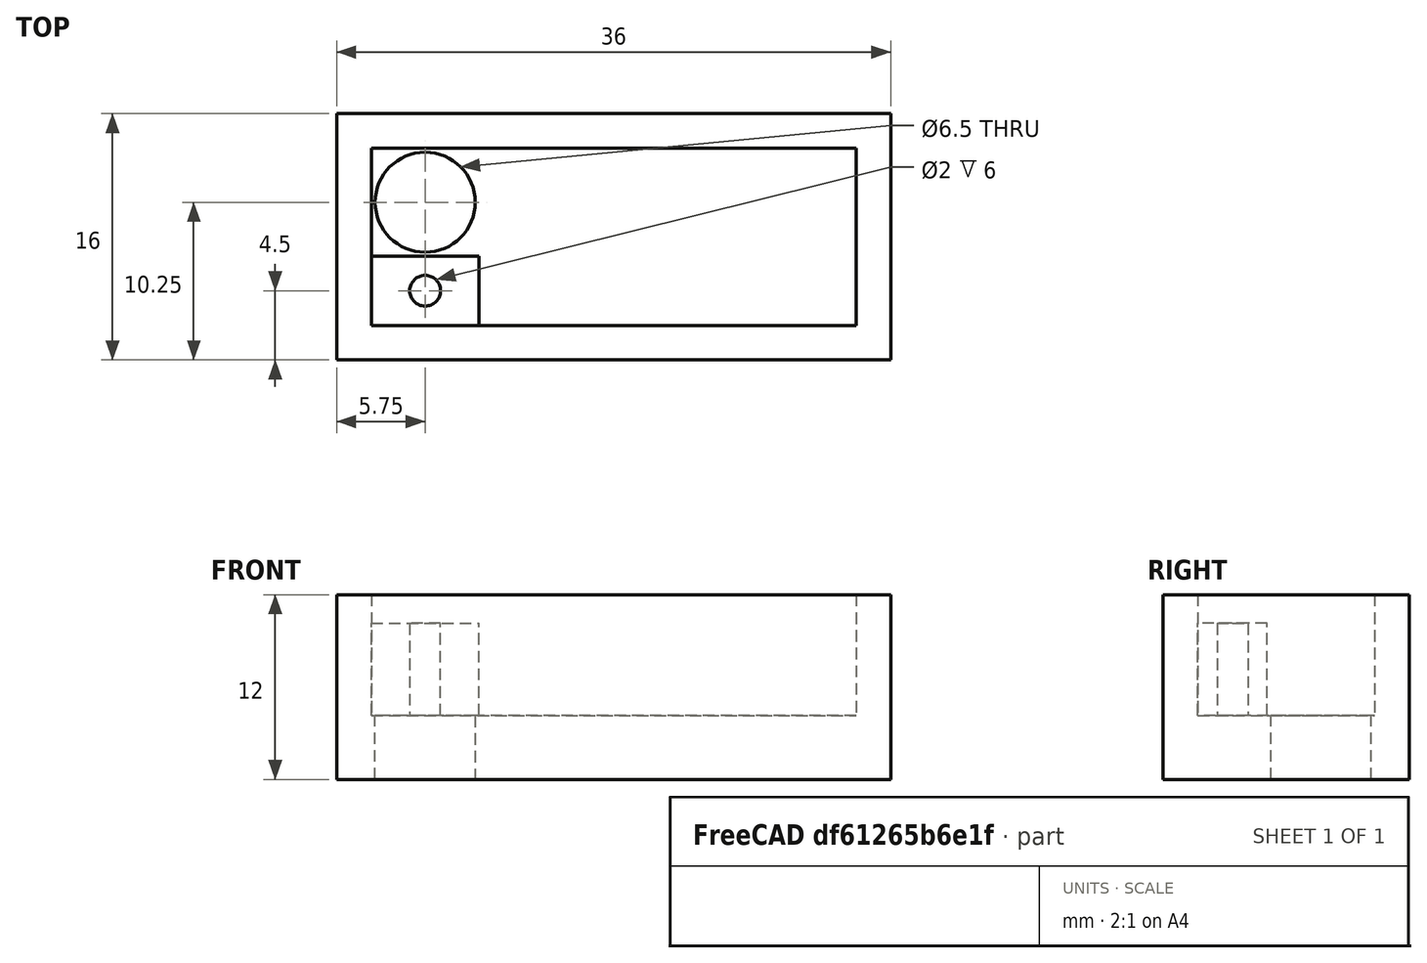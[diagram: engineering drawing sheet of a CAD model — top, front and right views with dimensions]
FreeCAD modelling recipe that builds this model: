
FCSTD DOCUMENT  (FreeCAD 0.19R24267 +148 (Git))
Label: LED Halterung
License: All rights reserved
LicenseURL: http://en.wikipedia.org/wiki/All_rights_reserved
objects: TechDraw::DrawViewDimension×14, Sketcher::SketchObject×4, TechDraw::DrawProjGroupItem×4, PartDesign::Pad×2, PartDesign::Pocket×2, PartDesign::Body×1, TechDraw::DrawSVGTemplate×1, TechDraw::DrawProjGroup×1, TechDraw::DrawPage×1
note: 13 computed .brp shape members not serialized (recipe doc carries the construction recipe); baked Part::Feature solids carry a one-line shape summary decoded from their .brp

FEATURE [Sketcher::SketchObject] Sketch
  FullyConstrained = true
  MapMode = 5
  Support = -> [XY_Plane]
  sketch-geometry (4):
    g0: LineSegment StartX=0 StartY=0 StartZ=0 EndX=36 EndY=0 EndZ=0
    g1: LineSegment StartX=36 StartY=0 StartZ=0 EndX=36 EndY=16 EndZ=0
    g2: LineSegment StartX=36 StartY=16 StartZ=0 EndX=0 EndY=16 EndZ=0
    g3: LineSegment StartX=0 StartY=16 StartZ=0 EndX=0 EndY=0 EndZ=0
  constraints (11):
    c: Coincident(g0,g1)
    c: Coincident(g1,g2)
    c: Coincident(g2,g3)
    c: Coincident(g3,g0)
    c: Horizontal(g0)
    c: Horizontal(g2)
    c: Vertical(g1)
    c: Vertical(g3)
    c: Coincident(g0,g-1)
    c: DistanceY(g3,g3) = 16
    c: DistanceX(g2,g2) = 36
FEATURE [PartDesign::Pad] Pad
  Direction = (1,1,1)
  Length = 12
  Length2 = 100
  Profile = -> Sketch
  Type = 0
FEATURE [Sketcher::SketchObject] Sketch001
  ExternalGeometry = -> [Pad]
  FullyConstrained = true
  MapMode = 5
  Placement = pos=(0,0,12) rot=(0,0,1;0rad)
  Support = -> [Pad]
  sketch-geometry (6):
    g0: LineSegment StartX=0 StartY=8 StartZ=0 EndX=36 EndY=8 EndZ=0
    g1: LineSegment StartX=18 StartY=16 StartZ=0 EndX=18 EndY=0 EndZ=0
    g2: LineSegment StartX=2.25 StartY=13.75 StartZ=0 EndX=33.75 EndY=13.75 EndZ=0
    g3: LineSegment StartX=33.75 StartY=13.75 StartZ=0 EndX=33.75 EndY=2.25 EndZ=0
    g4: LineSegment StartX=33.75 StartY=2.25 StartZ=0 EndX=2.25 EndY=2.25 EndZ=0
    g5: LineSegment StartX=2.25 StartY=2.25 StartZ=0 EndX=2.25 EndY=13.75 EndZ=0
  constraints (16):
    c: PointOnObject(g0,g-5)
    c: Horizontal(g0)
    c: PointOnObject(g1,g-3)
    c: Vertical(g1)
    c: Symmetric(g-1,g-4,g1)
    c: Symmetric(g-4,g-3,g0)
    c: Coincident(g2,g3)
    c: Coincident(g3,g4)
    c: Coincident(g4,g5)
    c: Coincident(g5,g2)
    c: Vertical(g5)
    c: Horizontal(g2)
    c: Symmetric(g3,g4,g1)
    c: Symmetric(g3,g2,g0)
    c: DistanceY(g2,g-5) = 2.25
    c: DistanceX(g-5,g2) = 2.25
FEATURE [PartDesign::Pocket] Pocket
  BaseFeature = -> Pad
  Length = 7.85
  Length2 = 100
  Profile = -> Sketch001
  Type = 0
FEATURE [Sketcher::SketchObject] Sketch002
  ExternalGeometry = -> [Pocket]
  FullyConstrained = true
  MapMode = 5
  Placement = pos=(0,0,4.15) rot=(0,0,1;0rad)
  Support = -> [Pocket]
  sketch-geometry (5):
    g0: LineSegment StartX=2.25 StartY=2.25 StartZ=0 EndX=9.25 EndY=2.25 EndZ=0
    g1: LineSegment StartX=9.25 StartY=2.25 StartZ=0 EndX=9.25 EndY=6.75 EndZ=0
    g2: LineSegment StartX=9.25 StartY=6.75 StartZ=0 EndX=2.25 EndY=6.75 EndZ=0
    g3: LineSegment StartX=2.25 StartY=6.75 StartZ=0 EndX=2.25 EndY=2.25 EndZ=0
    g4: Circle CenterX=5.75 CenterY=4.5 CenterZ=0 NormalX=0 NormalY=0 NormalZ=1 AngleXU=0 Radius=1
  constraints (13):
    c: Coincident(g0,g1)
    c: Coincident(g1,g2)
    c: Coincident(g2,g3)
    c: Coincident(g3,g0)
    c: Horizontal(g0)
    c: Horizontal(g2)
    c: Vertical(g1)
    c: Vertical(g3)
    c: Coincident(g0,g-5)
    c: DistanceY(g0,g4) = 2.25
    c: DistanceX(g0,g4) = 3.5
    c: Radius(g4) = 1
    c: Symmetric(g0,g1,g4)
FEATURE [PartDesign::Pad] Pad001
  BaseFeature = -> Pocket
  Direction = (1,1,1)
  Length = 6
  Length2 = 100
  Profile = -> Sketch002
  Type = 0
FEATURE [Sketcher::SketchObject] Sketch003
  ExternalGeometry = -> [Pad001]
  FullyConstrained = true
  MapMode = 5
  Placement = pos=(0,0,4.15) rot=(0,0,1;0rad)
  Support = -> [Pad001]
  sketch-geometry (1):
    g0: Circle CenterX=5.75 CenterY=10.25 CenterZ=0 NormalX=0 NormalY=0 NormalZ=1 AngleXU=0 Radius=3.25
  constraints (3):
    c: Vertical(g0,g-6)
    c: DistanceY(g0,g-5) = 3.5
    c: Radius(g0) = 3.25
FEATURE [PartDesign::Pocket] Pocket001
  BaseFeature = -> Pad001
  Length = 5
  Length2 = 100
  Profile = -> Sketch003
  Type = 0
FEATURE [PartDesign::Body] Body
  Group = -> [Sketch,Pad,Sketch001,Pocket,Sketch002,Pad001,Sketch003,Pocket001]
  Origin = -> Origin
  Tip = -> Pocket001
FEATURE [TechDraw::DrawSVGTemplate] Template
  EditableTexts = Designed_by_Name=David Völlm; Drawing_number=1; FC-Date=Date; FC-SC=1:1; FC-SH=1; FC-Title=LED-Halterung; Subtitle=Subtitle; Weight=Weight
  Height = 210
  Orientation = 1
  Width = 297
FEATURE [TechDraw::DrawProjGroupItem] ProjItem  label="Front"
  CoarseView = false
  Direction = (0,-1,0)
  Focus = 100
  HardHidden = false
  IsoCount = 0
  IsoHidden = false
  IsoVisible = false
  LockPosition = true
  Perspective = false
  Rotation = 0
  RotationVector = (1,0,0)
  ScaleType = 2
  SeamHidden = false
  SeamVisible = true
  SmoothHidden = false
  SmoothVisible = true
  Source = -> [Body]
  Type = 0
  X = 0
  XDirection = (1,0,0)
  Y = 0
FEATURE [TechDraw::DrawProjGroupItem] ProjItem001  label="Left"
  CoarseView = false
  Direction = (-1,-1e-16,0)
  Focus = 100
  HardHidden = false
  IsoCount = 0
  IsoHidden = false
  IsoVisible = false
  LockPosition = false
  Perspective = false
  Rotation = 0
  RotationVector = (1,0,0)
  ScaleType = 2
  SeamHidden = false
  SeamVisible = true
  SmoothHidden = false
  SmoothVisible = true
  Source = -> [Body]
  Type = 1
  X = 41
  XDirection = (1e-16,-1,0)
  Y = 0
FEATURE [TechDraw::DrawProjGroupItem] ProjItem002  label="Bottom"
  CoarseView = false
  Direction = (0,0,-1)
  Focus = 100
  HardHidden = false
  IsoCount = 0
  IsoHidden = false
  IsoVisible = false
  LockPosition = false
  Perspective = false
  Rotation = 0
  RotationVector = (1,0,0)
  ScaleType = 2
  SeamHidden = false
  SeamVisible = true
  SmoothHidden = false
  SmoothVisible = true
  Source = -> [Body]
  Type = 5
  X = 0
  XDirection = (1,0,0)
  Y = 31
FEATURE [TechDraw::DrawProjGroupItem] ProjItem003  label="Top"
  CoarseView = false
  Direction = (0,0,1)
  Focus = 100
  HardHidden = false
  IsoCount = 0
  IsoHidden = false
  IsoVisible = false
  LockPosition = false
  Perspective = false
  Rotation = 0
  RotationVector = (1,0,0)
  ScaleType = 2
  SeamHidden = false
  SeamVisible = true
  SmoothHidden = false
  SmoothVisible = true
  Source = -> [Body]
  Type = 4
  X = 0
  XDirection = (1,0,0)
  Y = -31
FEATURE [TechDraw::DrawProjGroup] ProjGroup
  Anchor = -> ProjItem
  AutoDistribute = true
  LockPosition = false
  ProjectionType = 0
  Rotation = 0
  ScaleType = 0
  Source = -> [Body]
  Views = -> [ProjItem,ProjItem001,ProjItem002,ProjItem003]
  X = 99.7152
  Y = 125.018
  spacingX = 15
  spacingY = 15
FEATURE [TechDraw::DrawViewDimension] Dimension
  Arbitrary = false
  ArbitraryTolerances = false
  EqualTolerance = true
  FormatSpec = R%.2f
  FormatSpecOverTolerance = %+.2f
  FormatSpecUnderTolerance = %+.2f
  Inverted = false
  LockPosition = false
  MeasureType = 1
  OverTolerance = 0
  References2D = -> [ProjItem002]
  Rotation = 0
  ScaleType = 0
  TheoreticalExact = false
  Type = 4
  UnderTolerance = 0
  X = 6.31337
  Y = 3.55127
FEATURE [TechDraw::DrawViewDimension] Dimension001
  Arbitrary = false
  ArbitraryTolerances = false
  EqualTolerance = true
  FormatSpec = %.2f
  FormatSpecOverTolerance = %+.2f
  FormatSpecUnderTolerance = %+.2f
  Inverted = false
  LockPosition = false
  MeasureType = 1
  OverTolerance = 0
  References2D = -> [ProjItem002]
  Rotation = 0
  ScaleType = 0
  TheoreticalExact = false
  Type = 2
  UnderTolerance = 0
  X = 25.1025
  Y = 1.97293
FEATURE [TechDraw::DrawViewDimension] Dimension002
  Arbitrary = false
  ArbitraryTolerances = false
  EqualTolerance = true
  FormatSpec = %.2f
  FormatSpecOverTolerance = %+.2f
  FormatSpecUnderTolerance = %+.2f
  Inverted = false
  LockPosition = false
  MeasureType = 1
  OverTolerance = 0
  References2D = -> [ProjItem002]
  Rotation = 0
  ScaleType = 0
  TheoreticalExact = false
  Type = 1
  UnderTolerance = 0
  X = -1.57834
  Y = 23.7834
FEATURE [TechDraw::DrawViewDimension] Dimension003
  Arbitrary = false
  ArbitraryTolerances = false
  EqualTolerance = true
  FormatSpec = %.2f
  FormatSpecOverTolerance = %+.2f
  FormatSpecUnderTolerance = %+.2f
  Inverted = false
  LockPosition = false
  MeasureType = 1
  OverTolerance = 0
  References2D = -> [ProjItem002]
  Rotation = 0
  ScaleType = 0
  TheoreticalExact = false
  Type = 1
  UnderTolerance = 0
  X = -13.8946
  Y = -13.0167
FEATURE [TechDraw::DrawViewDimension] Dimension004
  Arbitrary = false
  ArbitraryTolerances = false
  EqualTolerance = true
  FormatSpec = %.2f
  FormatSpecOverTolerance = %+.2f
  FormatSpecUnderTolerance = %+.2f
  Inverted = false
  LockPosition = false
  MeasureType = 1
  OverTolerance = 0
  References2D = -> [ProjItem002]
  Rotation = 0
  ScaleType = 0
  TheoreticalExact = false
  Type = 2
  UnderTolerance = 0
  X = -31.6509
  Y = 7.50174
FEATURE [TechDraw::DrawViewDimension] Dimension005
  Arbitrary = false
  ArbitraryTolerances = false
  EqualTolerance = true
  FormatSpec = %.2f
  FormatSpecOverTolerance = %+.2f
  FormatSpecUnderTolerance = %+.2f
  Inverted = false
  LockPosition = false
  MeasureType = 1
  OverTolerance = 0
  References2D = -> [ProjItem001]
  Rotation = 0
  ScaleType = 0
  TheoreticalExact = false
  Type = 2
  UnderTolerance = 0
  X = 15.8917
  Y = 1.18376
FEATURE [TechDraw::DrawViewDimension] Dimension006
  Arbitrary = false
  ArbitraryTolerances = false
  EqualTolerance = true
  FormatSpec = %.2f
  FormatSpecOverTolerance = %+.2f
  FormatSpecUnderTolerance = %+.2f
  Inverted = false
  LockPosition = false
  MeasureType = 1
  OverTolerance = 0
  References2D = -> [ProjItem003]
  Rotation = 0
  ScaleType = 0
  TheoreticalExact = false
  Type = 2
  UnderTolerance = 0
  X = 23.3023
  Y = 1.4631
FEATURE [TechDraw::DrawViewDimension] Dimension007
  Arbitrary = false
  ArbitraryTolerances = false
  EqualTolerance = true
  FormatSpec = %.2f
  FormatSpecOverTolerance = %+.2f
  FormatSpecUnderTolerance = %+.2f
  Inverted = false
  LockPosition = false
  MeasureType = 1
  OverTolerance = 0
  References2D = -> [ProjItem003]
  Rotation = 0
  ScaleType = 0
  TheoreticalExact = false
  Type = 2
  UnderTolerance = 0
  X = 34.246
  Y = -0.603869
FEATURE [TechDraw::DrawViewDimension] Dimension008
  Arbitrary = false
  ArbitraryTolerances = false
  EqualTolerance = true
  FormatSpec = %.2f
  FormatSpecOverTolerance = %+.2f
  FormatSpecUnderTolerance = %+.2f
  Inverted = false
  LockPosition = false
  MeasureType = 1
  OverTolerance = 0
  References2D = -> [ProjItem003]
  Rotation = 0
  ScaleType = 0
  TheoreticalExact = false
  Type = 1
  UnderTolerance = 0
  X = 10.7951
  Y = -9.48066
FEATURE [TechDraw::DrawViewDimension] Dimension009
  Arbitrary = false
  ArbitraryTolerances = false
  EqualTolerance = true
  FormatSpec = %.2f
  FormatSpecOverTolerance = %+.2f
  FormatSpecUnderTolerance = %+.2f
  Inverted = false
  LockPosition = false
  MeasureType = 1
  OverTolerance = 0
  References2D = -> [ProjItem003]
  Rotation = 0
  ScaleType = 0
  TheoreticalExact = false
  Type = 1
  UnderTolerance = 0
  X = 4.10387
  Y = -16.0816
FEATURE [TechDraw::DrawViewDimension] Dimension010
  Arbitrary = false
  ArbitraryTolerances = false
  EqualTolerance = true
  FormatSpec = %.2f
  FormatSpecOverTolerance = %+.2f
  FormatSpecUnderTolerance = %+.2f
  Inverted = false
  LockPosition = false
  MeasureType = 1
  OverTolerance = 0
  References2D = -> [ProjItem003]
  Rotation = 0
  ScaleType = 0
  TheoreticalExact = false
  Type = 1
  UnderTolerance = 0
  X = 2.68016
  Y = -24.5107
FEATURE [TechDraw::DrawViewDimension] Dimension011
  Arbitrary = false
  ArbitraryTolerances = false
  EqualTolerance = true
  FormatSpec = %.2f
  FormatSpecOverTolerance = %+.2f
  FormatSpecUnderTolerance = %+.2f
  Inverted = false
  LockPosition = false
  MeasureType = 1
  OverTolerance = 0
  References2D = -> [ProjItem003]
  Rotation = 0
  ScaleType = 0
  TheoreticalExact = false
  Type = 1
  UnderTolerance = 0
  X = -0.264683
  Y = -32.4104
FEATURE [TechDraw::DrawViewDimension] Dimension012
  Arbitrary = false
  ArbitraryTolerances = false
  EqualTolerance = true
  FormatSpec = %.2f
  FormatSpecOverTolerance = %+.2f
  FormatSpecUnderTolerance = %+.2f
  Inverted = false
  LockPosition = false
  MeasureType = 1
  OverTolerance = 0
  References2D = -> [ProjItem003]
  Rotation = 0
  ScaleType = 0
  TheoreticalExact = false
  Type = 1
  UnderTolerance = 0
  X = -1.04226
  Y = -40.6576
FEATURE [TechDraw::DrawViewDimension] Dimension013
  Arbitrary = false
  ArbitraryTolerances = false
  EqualTolerance = true
  FormatSpec = R%.2f
  FormatSpecOverTolerance = %+.2f
  FormatSpecUnderTolerance = %+.2f
  Inverted = false
  LockPosition = false
  MeasureType = 1
  OverTolerance = 0
  References2D = -> [ProjItem003]
  Rotation = 0
  ScaleType = 0
  TheoreticalExact = false
  Type = 4
  UnderTolerance = 0
  X = -33.1787
  Y = 3.82163
FEATURE [TechDraw::DrawPage] Page
  KeepUpdated = true
  NextBalloonIndex = 1
  ProjectionType = 0
  Template = -> Template
  Views = -> [ProjGroup,Dimension,Dimension001,Dimension002,Dimension003,Dimension004,Dimension005,Dimension006,Dimension007,Dimension008,Dimension009,Dimension010,Dimension011,Dimension012,Dimension013]
